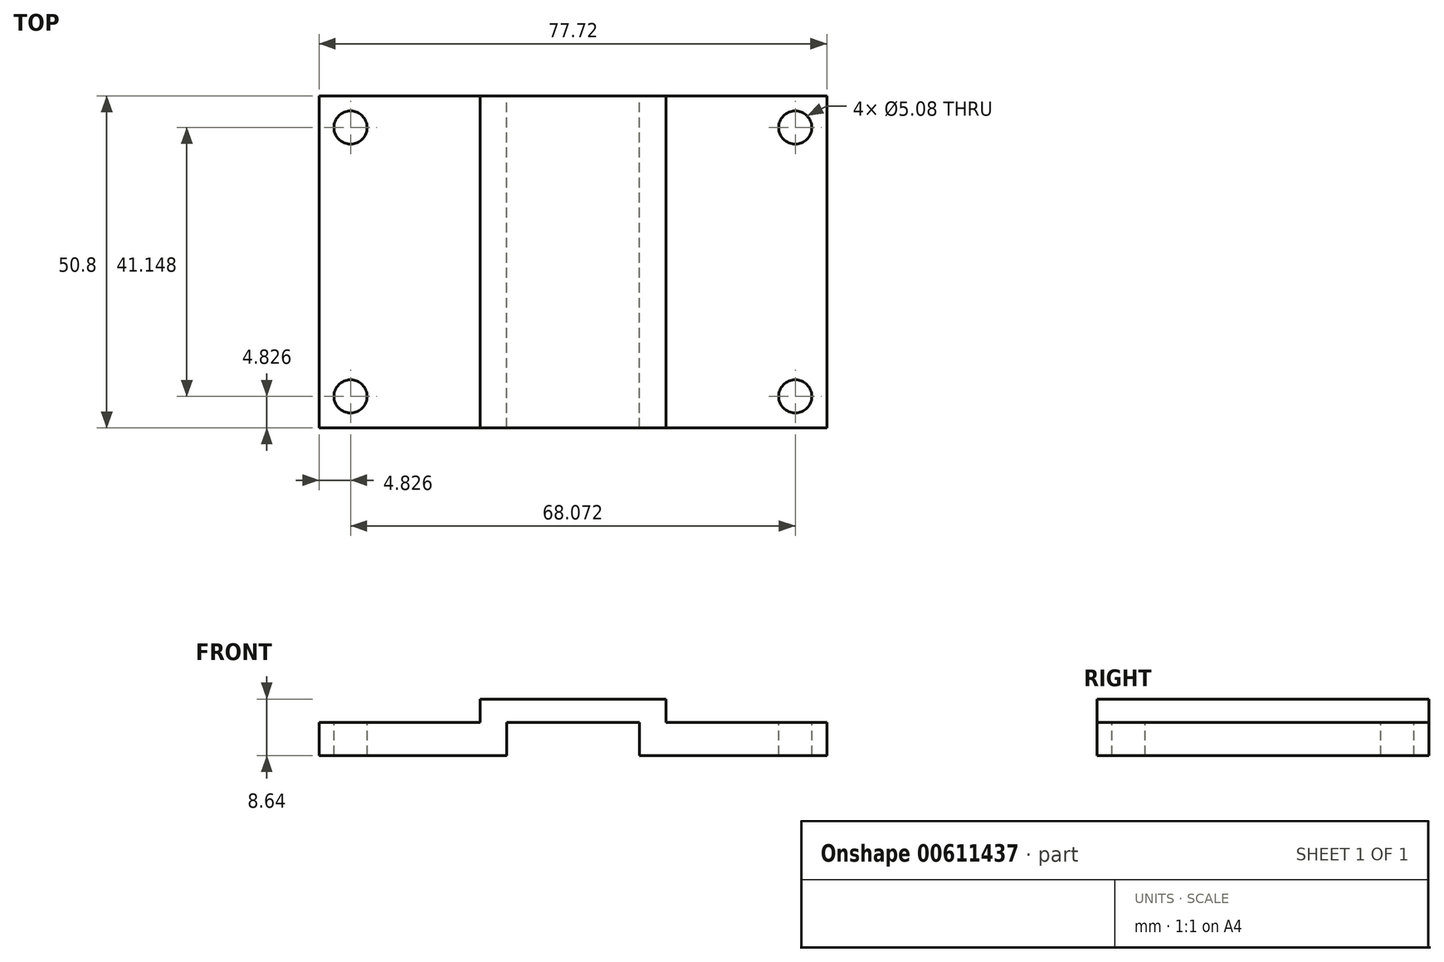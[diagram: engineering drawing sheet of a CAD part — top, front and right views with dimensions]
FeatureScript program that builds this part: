
annotation { "Feature Type Name" : "Feature", "Feature Type Description" : "" }
export const myFeature = defineFeature(function(context is Context, id is Id, definition is map)
    precondition{}
    {
        {
            var Q0;
            Q0=qCreatedBy(makeId("Front.planeOp"),FACE);
            var sketch = newSketch(context, id + "F0", { "sketchPlane" : qUnion([Q0])});
            skLineSegment(sketch, "E0", {"start": v(0, 0) * mm, "end": v(28.7, 0) * mm});
            skLineSegment(sketch, "E1", {"start": v(28.7, 0) * mm, "end": v(28.7, 5.08) * mm});
            skLineSegment(sketch, "E2", {"start": v(28.7, 5.08) * mm, "end": v(49.02, 5.08) * mm});
            skLineSegment(sketch, "E3", {"start": v(49.02, 5.08) * mm, "end": v(49.02, 0) * mm});
            skLineSegment(sketch, "E4", {"start": v(49.02, 0) * mm, "end": v(77.72, 0) * mm});
            skLineSegment(sketch, "E5", {"start": v(77.72, 0) * mm, "end": v(77.72, 5.08) * mm});
            skLineSegment(sketch, "E6", {"start": v(77.72, 5.08) * mm, "end": v(53.09, 5.08) * mm});
            skLineSegment(sketch, "E7", {"start": v(53.09, 5.08) * mm, "end": v(53.09, 8.64) * mm});
            skLineSegment(sketch, "E8", {"start": v(53.09, 8.64) * mm, "end": v(24.64, 8.64) * mm});
            skLineSegment(sketch, "E9", {"start": v(24.64, 8.64) * mm, "end": v(24.64, 5.08) * mm});
            skLineSegment(sketch, "E10", {"start": v(24.64, 5.08) * mm, "end": v(0, 5.08) * mm});
            skLineSegment(sketch, "E11", {"start": v(0, 5.08) * mm, "end": v(0, 0) * mm});
            skSolve(sketch);
        }
        {
            var Q0;
            Q0 = qSketchRegion(id + "F0", true);
            extrude(context, id + "F1", {"entities" : qUnion([Q0]), "depth" : 50.8 * mm, "offsetDistance" : 25.4 * mm});
        }
        {
            var Q0;
            Q0=makeQuery(id+"F1.opExtrude","SWEPT_FACE",FACE,{"disambiguationData":[OSD([sQuery(id+"F0.wireOp",EDGE,"E10")])]});
            var sketch = newSketch(context, id + "F2", { "sketchPlane" : qUnion([Q0])});
            skCircle(sketch, "E12", {"center": v(4.83, -4.83) * mm, "radius": 2.54 * mm});
            skCircle(sketch, "E13", {"center": v(4.83, -45.97) * mm, "radius": 2.54 * mm});
            skCircle(sketch, "E14", {"center": v(72.9, -45.97) * mm, "radius": 2.54 * mm});
            skCircle(sketch, "E15", {"center": v(72.9, -4.83) * mm, "radius": 2.54 * mm});
            skSolve(sketch);
        }
        {
            var Q0;
            Q0 = qSketchRegion(id + "F2", true);
            extrude(context, id + "F3", {"entities" : qUnion([Q0]), "operationType" : NewBodyOperationType.REMOVE, "endBound" : BoundingType.THROUGH_ALL, "oppositeDirection" : true, "depth" : 25.4 * mm, "offsetDistance" : 25.4 * mm});
        }
    });
